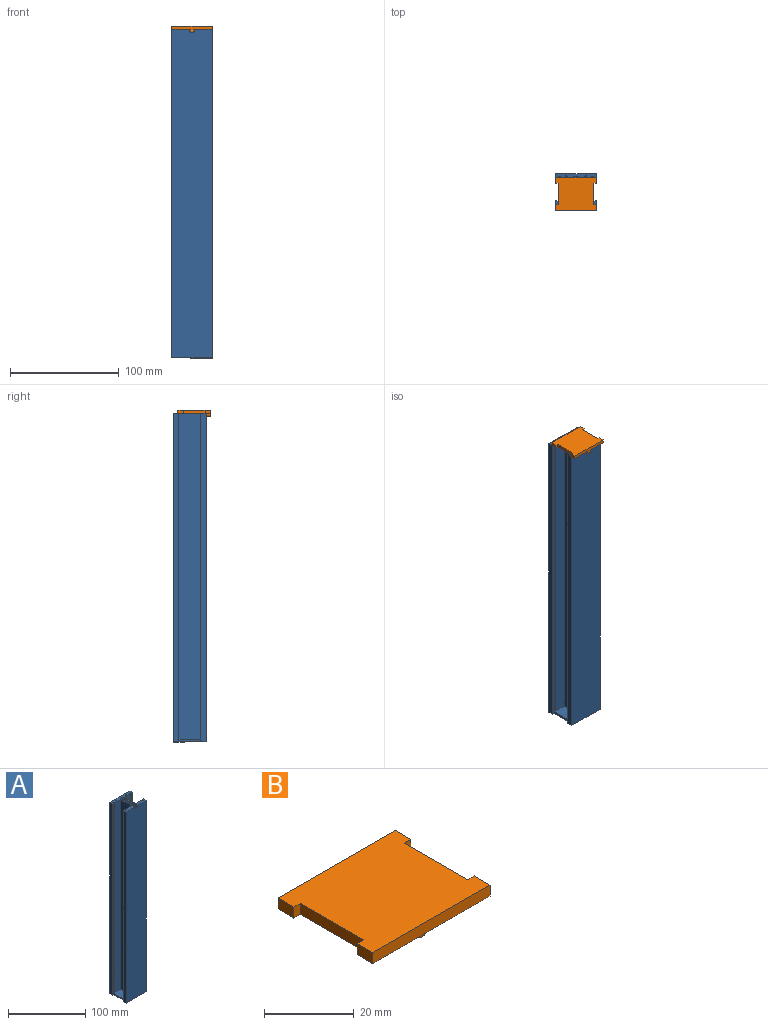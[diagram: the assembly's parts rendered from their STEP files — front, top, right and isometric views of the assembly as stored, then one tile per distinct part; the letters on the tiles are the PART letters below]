
ASSEMBLY  parts=2 mates=1
PART A: 46 faces, bbox 37x30x302.5 mm
  f0: plane 37x30mm, normal (0,0,1), area 360.5mm2, adj f3,f4,f5,f6,f7,f9,f10,f11
  f1: plane 23x13mm, normal (0,0,1), area 266mm2, adj f8,f21,f22,f23,f24,f25,f26,f27
  f2: plane 20x2mm, normal (1,0,0), area 40mm2, adj f3,f13,f14,f15
  f3: plane 302.5x2mm, normal (0,-1,0), area 605mm2, adj f0,f2,f4,f15,f20
  f4: plane 302.5x5mm, normal (1,0,0), area 1512.5mm2, adj f0,f3,f5,f15
  f5: plane 302.5x37mm, normal (0,1,0), area 11192.5mm2, adj f0,f4,f6,f15
  f6: plane 302.5x5mm, normal (-1,0,0), area 1512.5mm2, adj f0,f5,f7,f15
  f7: plane 302.5x2mm, normal (0,-1,0), area 605mm2, adj f0,f6,f8,f15,f21
  f8: plane 20x2mm, normal (-1,0,0), area 40mm2, adj f1,f7,f9,f15
  f9: plane 302.5x2mm, normal (0,1,0), area 605mm2, adj f0,f8,f10,f15,f29
  f10: plane 302.5x5mm, normal (-1,0,0), area 1512.5mm2, adj f0,f9,f11,f15
  f11: plane 302.5x37mm, normal (0,-1,0), area 11180.8mm2, adj f0,f10,f12,f15,f38,f40,f41
  f12: plane 302.5x5mm, normal (1,0,0), area 1512.5mm2, adj f0,f11,f13,f15
  f13: plane 302.5x2mm, normal (0,1,0), area 605mm2, adj f0,f2,f12,f15,f30
  f14: plane 23x13mm, normal (0,0,1), area 266mm2, adj f2,f16,f17,f18,f19,f20,f30,f31
  f15: plane 37x30mm, normal (0,0,-1), area 1030mm2, adj f2,f3,f4,f5,f6,f7,f8,f9
  f16: plane 300.5x20mm, normal (1,0,0), area 6010mm2, adj f0,f14,f17,f33
  f17: plane 300.5x11mm, normal (0,-1,0), area 3305.5mm2, adj f0,f14,f16,f18
  f18: plane 300.5x2.5mm, normal (1,0,0), area 451.7mm2, adj f0,f14,f17,f19,f36
  f19: plane 298.5x2mm, normal (0,-1,0), area 597mm2, adj f14,f18,f20,f36
  f20: plane 300.5x2.5mm, normal (-1,0,0), area 451.8mm2, adj f0,f3,f14,f19,f36
  f21: plane 300.5x2.5mm, normal (1,0,0), area 451.8mm2, adj f0,f1,f7,f22,f37
  f22: plane 298.5x2mm, normal (0,-1,0), area 597mm2, adj f1,f21,f23,f37
  f23: plane 300.5x2.5mm, normal (-1,0,0), area 451.7mm2, adj f0,f1,f22,f24,f37
  f24: plane 300.5x11mm, normal (0,-1,0), area 3305.5mm2, adj f0,f1,f23,f25
  f25: plane 300.5x20mm, normal (-1,0,0), area 6010mm2, adj f0,f1,f24,f26
  f26: plane 300.5x11mm, normal (0,1,0), area 3305.5mm2, adj f0,f1,f25,f27
  f27: plane 300.5x2.5mm, normal (-1,0,0), area 451.7mm2, adj f0,f1,f26,f28,f34
  f28: plane 298.5x2mm, normal (0,1,0), area 597mm2, adj f1,f27,f29,f34
  f29: plane 300.5x2.5mm, normal (1,0,0), area 451.8mm2, adj f0,f1,f9,f28,f34
  f30: plane 300.5x2.5mm, normal (-1,0,0), area 451.8mm2, adj f0,f13,f14,f31,f35
  f31: plane 298.5x2mm, normal (0,1,0), area 597mm2, adj f14,f30,f32,f35
  f32: plane 300.5x2.5mm, normal (1,0,0), area 451.7mm2, adj f0,f14,f31,f33,f35
  f33: plane 300.5x11mm, normal (0,1,0), area 3305.5mm2, adj f0,f14,f16,f32
  f34: plane 2x2mm, normal (0,0.89,0.45), area 4.5mm2, adj f0,f27,f28,f29
  f35: plane 2x2mm, normal (0,0.89,0.45), area 4.5mm2, adj f0,f30,f31,f32
  f36: plane 2x2mm, normal (0,-0.89,0.45), area 4.5mm2, adj f0,f18,f19,f20
  f37: plane 2x2mm, normal (0,-0.89,0.45), area 4.5mm2, adj f0,f21,f22,f23
  f38: cylinder r=2mm len=27mm, axis (0,-1,0), area 209.4mm2, adj f11,f39,f40,f41
  f39: plane 4.66x3.4mm, normal (0,-1,0), area 11.7mm2, adj f0,f38,f40,f41
  f40: cylinder r=0.5mm len=27mm, axis (0,-1,0), area 26.2mm2, adj f0,f11,f38,f39
  f41: cylinder r=0.5mm len=27mm, axis (0,-1,0), area 26.2mm2, adj f0,f11,f38,f39
  f42: cylinder r=0.75mm len=1.5mm, axis (0,0,1), area 4.7mm2, adj f0,f43
  f43: plane 1.5x1.5mm, normal (0,0,1), area 1.8mm2, adj f42
  f44: cylinder r=0.75mm len=1.5mm, axis (0,0,1), area 4.7mm2, adj f0,f45
  f45: plane 1.5x1.5mm, normal (0,0,1), area 1.8mm2, adj f44
PART B: 20 faces, bbox 37x30x6.4 mm
  f0: plane 20x3mm, normal (1,0,0), area 60mm2, adj f1,f11,f12,f13
  f1: plane 3x2mm, normal (0,-1,0), area 6mm2, adj f0,f2,f12,f13
  f2: plane 5x3mm, normal (1,0,0), area 15mm2, adj f1,f3,f12,f13
  f3: plane 37x6.4mm, normal (0,1,0), area 122.4mm2, adj f2,f4,f12,f13,f14
  f4: plane 5x3mm, normal (-1,0,0), area 15mm2, adj f3,f5,f12,f13
  f5: plane 3x2mm, normal (0,-1,0), area 6mm2, adj f4,f6,f12,f13
  f6: plane 20x3mm, normal (-1,0,0), area 60mm2, adj f5,f7,f12,f13
  f7: plane 3x2mm, normal (0,1,0), area 6mm2, adj f6,f8,f12,f13
  f8: plane 5x3mm, normal (-1,0,0), area 15mm2, adj f7,f9,f12,f13
  f9: plane 37x3mm, normal (0,-1,0), area 111mm2, adj f8,f10,f12,f13
  f10: plane 5x3mm, normal (1,0,0), area 15mm2, adj f9,f11,f12,f13
  f11: plane 3x2mm, normal (0,1,0), area 6mm2, adj f0,f10,f12,f13
  f12: plane 37x30mm, normal (0,0,1), area 1030mm2, adj f0,f1,f2,f3,f4,f5,f6,f7
  f13: plane 37x30mm, normal (0,0,-1), area 949.3mm2, adj f0,f1,f2,f3,f4,f5,f6,f7
  f14: cylinder r=2mm len=27mm, axis (0,1,0), area 253.4mm2, adj f3,f13,f15
  f15: plane 4x3.4mm, normal (0,-1,0), area 11.4mm2, adj f13,f14
  f16: plane 0.5x0.5mm, normal (0,0,-1), area 0.2mm2, adj f19
  f17: plane 0.5x0.5mm, normal (0,0,-1), area 0.2mm2, adj f18
  f18: torus R=0.25mm, axis (0,0,-1), area 2.8mm2, adj f13,f17
  f19: torus R=0.25mm, axis (0,0,-1), area 2.8mm2, adj f13,f16
PLACE A t=(-25.4,3.78,72.25)mm
PLACE B rot(axis=(0,0,1),180deg) t=(-23.64,-0.94,374.75)mm
MATE slider B.f14 <-> A.f38  axis (0,-1,0) through (-25.4,-1.66,373.35)mm
